# Revit family: Sanitary_Bidets_Sanindusa_Sanlife-Wall-Mounted-Bidet
name_source: partatom
category: Plumbing Fixtures
revit_build: Autodesk Revit 2018 (Build: 20170223_1515(x64)
units: mm (PartAtom-declared; Revit-internal decimal feet)

## family parameters
Always vertical = Yes
Cut with Voids When Loaded = No
Host = Wall
OmniClass Number = 23.45.00.00
OmniClass Title = Sanitary, Laundry, and Cleaning Equipment
Part Type = Normal
Room Calculation Point = No
Round Connector Dimension = Use Diameter
Shared = No

## types (1)
- Sanitary_Bidets_Sanindusa_Sanlife-Wall-Mounted-Bidet
    AssetType = Fixed
    BIMObjectName = Bidet_Sanlife
    BidetMounting = wallhung
    Category = Pr_40_20_06_11,Bidets
    CodePerformance = EN 14528:2007 - CL 25
    Color = White
    Constituents = Compatible suport frames (not inluded): 439-Metal support for wall mounted bidet for pladur, 430-Metal support for wall mounted bidet. 48011-chromed embellishment ring (included)
    Cost = 0 $
    Description = Waste water appliance for washing the excretory organs while sitting astride the bowl (BS6100)
    DrainSize = 46 mm  [stored 0.150919 ft]
    Edition number = 1
    Element Type = BIDET: Waste water appliance for washing the excretory organs while sitting astride the bowl (BS6100)
    Features = Wall mounted bidet, easy to clean. Domestic and hotel use.
    Finish = Gloss
    InletDiameter = 35 mm
    Installation Instructions = https://www.tec.sanindusa.pt
    InstallationDate = 1900-12-31T23:59:59
    Manufacturer = Sanindusa
    ManufacturerName = Sanindusa
    ManufacturerURL = http://www.sanindusa.pt
    Material = Vitreous China
    ModelNumber = 136450004
    ModelReference = Sanlife
    Name = Bidet_Sanlife
    NominalHeight = 290 mm
    NominalLength = 380 mm
    NominalWidth = 560 mm
    Pre-defined type (IFC) = BIDET
    Product Guid = ba7e486c-1875-4d9d-9896-1d32552cc438
    Product data url = https://bimobject.com
    ProductInformation = https://www.tec.sanindusa.pt
    ProductionYear = 2018
    Size = 380x560x290
    SpilloverLevel = 102
    SustainabilityPerformance = n/a
n/a
    Type (IFC) = IfcSanitaryTerminalType
    URL = http://www.sanindusa.pt
    Uniclass2015Code = Pr_40_20_06_11
    Uniclass2015Title = Bidets
    Uniclass2015Version = Products v1.6
    Version = 1
    WarrantyDescription = https://www.tec.sanindusa.pt
    WarrantyDurationParts = 5
    WarrantyDurationUnit = year
    WarrantyStartDate = 1900-12-31T23:59:59
    Weight = 22.00 kg

note: [stored X ft] marks values corroborated as IEEE doubles in the binary element streams (Revit-internal decimal feet)

## geometry (parser evidence)
native form markers: Sweep x7
no freeform markers — native parametric forms only
